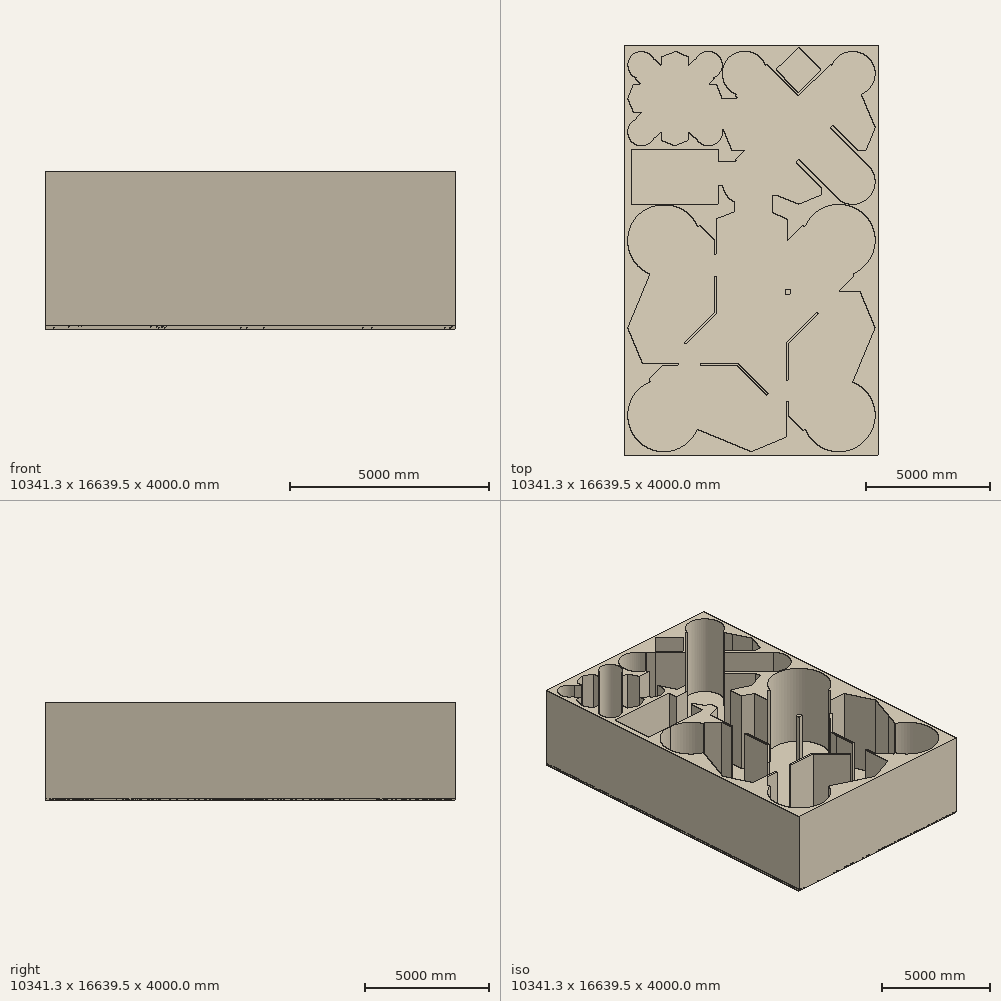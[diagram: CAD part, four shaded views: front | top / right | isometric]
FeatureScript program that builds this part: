
annotation { "Feature Type Name" : "Feature", "Feature Type Description" : "" }
export const myFeature = defineFeature(function(context is Context, id is Id, definition is map)
    precondition{}
    {
        {
            var Q0;
            Q0=qCreatedBy(makeId("Top.planeOp"),FACE);
            var sketch = newSketch(context, id + "F0", { "sketchPlane" : qUnion([Q0])});
            skLineSegment(sketch, "E0", {"start": v(2904.54, 7239.39) * mm, "end": v(3203.1, 7544.71) * mm});
            skLineSegment(sketch, "E1", {"start": v(1018, 2247.97) * mm, "end": v(1926.78, 1871.54) * mm});
            skLineSegment(sketch, "E2", {"start": v(5170.65, 8319.76) * mm, "end": v(-5170.65, 8319.76) * mm});
            skLineSegment(sketch, "E3", {"start": v(-5170.65, 8319.76) * mm, "end": v(-5170.65, -8319.76) * mm});
            skLineSegment(sketch, "E4", {"start": v(-5170.65, -8319.76) * mm, "end": v(5170.65, -8319.76) * mm});
            skLineSegment(sketch, "E5", {"start": v(5170.65, -8319.76) * mm, "end": v(5170.65, 8319.76) * mm});
            skLineSegment(sketch, "E6", {"start": v(-680.22, 1966.34) * mm, "end": v(-680.22, 1871.54) * mm});
            skLineSegment(sketch, "E7", {"start": v(1925.72, 8240.34) * mm, "end": v(2834.63, 7310.89) * mm});
            skLineSegment(sketch, "E8", {"start": v(2834.63, 7310.89) * mm, "end": v(1905.17, 6401.98) * mm});
            skLineSegment(sketch, "E9", {"start": v(1905.17, 6401.98) * mm, "end": v(996.26, 7331.44) * mm});
            skLineSegment(sketch, "E10", {"start": v(996.26, 7331.44) * mm, "end": v(1925.72, 8240.34) * mm});
            skLineSegment(sketch, "E11", {"start": v(4644.22, 4065.52) * mm, "end": v(4321.24, 4065.52) * mm});
            skLineSegment(sketch, "E12", {"start": v(4321.24, 4065.52) * mm, "end": v(4653.11, 4065.52) * mm});
            skLineSegment(sketch, "E13", {"start": v(4653.11, 4065.52) * mm, "end": v(5029.54, 4974.3) * mm});
            skLineSegment(sketch, "E14", {"start": v(5029.54, 4974.3) * mm, "end": v(4644.22, 5883.08) * mm});
            skLineSegment(sketch, "E15", {"start": v(4644.22, 5883.08) * mm, "end": v(4488.3, 6259.5) * mm});
            skLineSegment(sketch, "E16", {"start": v(4488.3, 6259.5) * mm, "end": v(4459.65, 6328.68) * mm});
            skArc(sketch, "E17", {"start": v(4459.65, 6328.68) * mm, "mid": v(4754.48, 7810.89) * mm, "end": v(3272.27, 7516.06) * mm});
            skLineSegment(sketch, "E18", {"start": v(3272.27, 7516.06) * mm, "end": v(3203.1, 7544.71) * mm});
            skLineSegment(sketch, "E19", {"start": v(3203.1, 7544.71) * mm, "end": v(2904.54, 7239.39) * mm});
            skLineSegment(sketch, "E20", {"start": v(2904.54, 7239.39) * mm, "end": v(1903.59, 6260.57) * mm});
            skLineSegment(sketch, "E21", {"start": v(1903.59, 6260.57) * mm, "end": v(924.77, 7261.52) * mm});
            skLineSegment(sketch, "E22", {"start": v(924.77, 7261.52) * mm, "end": v(641.57, 7544.71) * mm});
            skLineSegment(sketch, "E23", {"start": v(641.57, 7544.71) * mm, "end": v(572.4, 7516.06) * mm});
            skArc(sketch, "E24", {"start": v(572.4, 7516.06) * mm, "mid": v(-915.1, 7816.2) * mm, "end": v(-614.98, 6328.68) * mm});
            skLineSegment(sketch, "E25", {"start": v(-614.98, 6328.68) * mm, "end": v(-643.63, 6259.5) * mm});
            skLineSegment(sketch, "E26", {"start": v(-643.63, 6259.5) * mm, "end": v(-543.3, 6159.17) * mm});
            skLineSegment(sketch, "E27", {"start": v(-543.3, 6159.17) * mm, "end": v(-1184.87, 6159.17) * mm});
            skLineSegment(sketch, "E28", {"start": v(-1184.87, 6159.17) * mm, "end": v(-1417.55, 6720.91) * mm});
            skLineSegment(sketch, "E29", {"start": v(-1417.55, 6720.91) * mm, "end": v(-1746.6, 6720.91) * mm});
            skLineSegment(sketch, "E30", {"start": v(-1746.6, 6720.91) * mm, "end": v(-1513.93, 6953.59) * mm});
            skLineSegment(sketch, "E31", {"start": v(-1513.93, 6953.59) * mm, "end": v(-1531.64, 6996.35) * mm});
            skArc(sketch, "E32", {"start": v(-1531.64, 6996.35) * mm, "mid": v(-1349.4, 7912.53) * mm, "end": v(-2265.59, 7730.3) * mm});
            skLineSegment(sketch, "E33", {"start": v(-2265.59, 7730.3) * mm, "end": v(-2308.35, 7748) * mm});
            skLineSegment(sketch, "E34", {"start": v(-2308.35, 7748) * mm, "end": v(-2541.02, 7515.33) * mm});
            skLineSegment(sketch, "E35", {"start": v(-2541.02, 7515.33) * mm, "end": v(-2541.02, 7844.38) * mm});
            skLineSegment(sketch, "E36", {"start": v(-2541.02, 7844.38) * mm, "end": v(-3064.43, 8077.06) * mm});
            skLineSegment(sketch, "E37", {"start": v(-3064.43, 8077.06) * mm, "end": v(-3664.5, 7844.38) * mm});
            skLineSegment(sketch, "E38", {"start": v(-3664.5, 7844.38) * mm, "end": v(-3664.5, 7515.33) * mm});
            skLineSegment(sketch, "E39", {"start": v(-3664.5, 7515.33) * mm, "end": v(-3897.18, 7748) * mm});
            skLineSegment(sketch, "E40", {"start": v(-3897.18, 7748) * mm, "end": v(-3939.94, 7730.3) * mm});
            skArc(sketch, "E41", {"start": v(-3939.94, 7730.3) * mm, "mid": v(-4851.28, 7907.24) * mm, "end": v(-4674.04, 6995.95) * mm});
            skLineSegment(sketch, "E42", {"start": v(-4674.04, 6995.95) * mm, "end": v(-4691.6, 6953.59) * mm});
            skLineSegment(sketch, "E43", {"start": v(-4691.6, 6953.59) * mm, "end": v(-4458.91, 6720.91) * mm});
            skLineSegment(sketch, "E44", {"start": v(-4458.91, 6720.91) * mm, "end": v(-4796.65, 6720.91) * mm});
            skLineSegment(sketch, "E45", {"start": v(-4796.65, 6720.91) * mm, "end": v(-5020.65, 6159.17) * mm});
            skLineSegment(sketch, "E46", {"start": v(-5020.65, 6159.17) * mm, "end": v(-4787.97, 5597.44) * mm});
            skLineSegment(sketch, "E47", {"start": v(-4787.97, 5597.44) * mm, "end": v(-4458.91, 5597.44) * mm});
            skLineSegment(sketch, "E48", {"start": v(-4458.91, 5597.44) * mm, "end": v(-4691.6, 5364.76) * mm});
            skLineSegment(sketch, "E49", {"start": v(-4691.6, 5364.76) * mm, "end": v(-4673.88, 5322) * mm});
            skArc(sketch, "E50", {"start": v(-4673.88, 5322) * mm, "mid": v(-4856.12, 4405.81) * mm, "end": v(-3939.94, 4588.05) * mm});
            skLineSegment(sketch, "E51", {"start": v(-3939.94, 4588.05) * mm, "end": v(-3897.18, 4570.34) * mm});
            skLineSegment(sketch, "E52", {"start": v(-3897.18, 4570.34) * mm, "end": v(-3664.5, 4803.02) * mm});
            skLineSegment(sketch, "E53", {"start": v(-3664.5, 4803.02) * mm, "end": v(-3664.5, 4473.96) * mm});
            skLineSegment(sketch, "E54", {"start": v(-3664.5, 4473.96) * mm, "end": v(-3102.76, 4241.28) * mm});
            skLineSegment(sketch, "E55", {"start": v(-3102.76, 4241.28) * mm, "end": v(-2541.02, 4473.96) * mm});
            skLineSegment(sketch, "E56", {"start": v(-2541.02, 4473.96) * mm, "end": v(-2541.02, 4803.02) * mm});
            skLineSegment(sketch, "E57", {"start": v(-2541.02, 4803.02) * mm, "end": v(-2308.35, 4570.34) * mm});
            skLineSegment(sketch, "E58", {"start": v(-2308.35, 4570.34) * mm, "end": v(-2265.59, 4588.05) * mm});
            skArc(sketch, "E59", {"start": v(-2265.59, 4588.05) * mm, "mid": v(-1544.96, 4276.78) * mm, "end": v(-1184.87, 4974.3) * mm});
            skLineSegment(sketch, "E60", {"start": v(-1184.87, 4974.3) * mm, "end": v(-1175.98, 4974.3) * mm});
            skLineSegment(sketch, "E61", {"start": v(-1175.98, 4974.3) * mm, "end": v(-799.55, 4065.52) * mm});
            skLineSegment(sketch, "E62", {"start": v(-799.55, 4065.52) * mm, "end": v(-267.2, 4065.52) * mm});
            skLineSegment(sketch, "E63", {"start": v(-267.2, 4065.52) * mm, "end": v(-643.63, 3689.1) * mm});
            skLineSegment(sketch, "E64", {"start": v(-643.63, 3689.1) * mm, "end": v(-623.87, 3619.92) * mm});
            skLineSegment(sketch, "E65", {"start": v(-623.87, 3619.92) * mm, "end": v(-1184.87, 3619.92) * mm});
            skLineSegment(sketch, "E66", {"start": v(-1184.87, 3619.92) * mm, "end": v(-1334.87, 3619.92) * mm});
            skLineSegment(sketch, "E67", {"start": v(-1334.87, 3619.92) * mm, "end": v(-1334.87, 4091.28) * mm});
            skLineSegment(sketch, "E68", {"start": v(-1334.87, 4091.28) * mm, "end": v(-4870.65, 4091.28) * mm});
            skLineSegment(sketch, "E69", {"start": v(-4870.65, 4091.28) * mm, "end": v(-4870.65, 1871.54) * mm});
            skLineSegment(sketch, "E70", {"start": v(-4870.65, 1871.54) * mm, "end": v(-1334.87, 1871.54) * mm});
            skLineSegment(sketch, "E71", {"start": v(-1334.87, 1871.54) * mm, "end": v(-1334.87, 2639.74) * mm});
            skLineSegment(sketch, "E72", {"start": v(-1334.87, 2639.74) * mm, "end": v(-1173.94, 2639.74) * mm});
            skArc(sketch, "E73", {"start": v(-1173.94, 2639.74) * mm, "mid": v(-1014.88, 2238.67) * mm, "end": v(-680.22, 1966.34) * mm});
            skLineSegment(sketch, "E74", {"start": v(-680.22, 1966.34) * mm, "end": v(-680.22, 1568.87) * mm});
            skLineSegment(sketch, "E75", {"start": v(-680.22, 1568.87) * mm, "end": v(-1411.63, 1285.27) * mm});
            skLineSegment(sketch, "E76", {"start": v(-1411.63, 1285.27) * mm, "end": v(-1411.63, -165.8) * mm});
            skLineSegment(sketch, "E77", {"start": v(-1411.63, -165.8) * mm, "end": v(-1511.63, -165.8) * mm});
            skLineSegment(sketch, "E78", {"start": v(-1511.63, -165.8) * mm, "end": v(-1511.63, 442.14) * mm});
            skLineSegment(sketch, "E79", {"start": v(-1511.63, 442.14) * mm, "end": v(-2079.62, 1010.13) * mm});
            skLineSegment(sketch, "E80", {"start": v(-2079.62, 1010.13) * mm, "end": v(-2189.27, 964.71) * mm});
            skArc(sketch, "E81", {"start": v(-2189.27, 964.71) * mm, "mid": v(-2692.58, 1598.76) * mm, "end": v(-3464.85, 1841.54) * mm});
            skArc(sketch, "E82", {"start": v(-3464.85, 1841.54) * mm, "mid": v(-4987.75, 718.48) * mm, "end": v(-4113.82, -959.83) * mm});
            skLineSegment(sketch, "E83", {"start": v(-4113.82, -959.83) * mm, "end": v(-4159.24, -1069.49) * mm});
            skLineSegment(sketch, "E84", {"start": v(-4159.24, -1069.49) * mm, "end": v(-4159.24, -1069.49) * mm});
            skLineSegment(sketch, "E85", {"start": v(-4159.24, -1069.49) * mm, "end": v(-4434.25, -1733.43) * mm});
            skLineSegment(sketch, "E86", {"start": v(-4434.25, -1733.43) * mm, "end": v(-5020.65, -3149.11) * mm});
            skLineSegment(sketch, "E87", {"start": v(-5020.65, -3149.11) * mm, "end": v(-4433.78, -4565.94) * mm});
            skLineSegment(sketch, "E88", {"start": v(-4433.78, -4565.94) * mm, "end": v(-2971.24, -4565.94) * mm});
            skLineSegment(sketch, "E89", {"start": v(-2971.24, -4565.94) * mm, "end": v(-2971.24, -4665.94) * mm});
            skLineSegment(sketch, "E90", {"start": v(-2971.24, -4665.94) * mm, "end": v(-3591.24, -4665.94) * mm});
            skLineSegment(sketch, "E91", {"start": v(-3591.24, -4665.94) * mm, "end": v(-4159.24, -5228.73) * mm});
            skLineSegment(sketch, "E92", {"start": v(-4159.24, -5228.73) * mm, "end": v(-4112.88, -5340.67) * mm});
            skArc(sketch, "E93", {"start": v(-4112.88, -5340.67) * mm, "mid": v(-4589.95, -7739.06) * mm, "end": v(-2191.56, -7261.99) * mm});
            skLineSegment(sketch, "E94", {"start": v(-2191.56, -7261.99) * mm, "end": v(-2079.62, -7308.35) * mm});
            skLineSegment(sketch, "E95", {"start": v(-2079.62, -7308.35) * mm, "end": v(-1470.51, -7560.65) * mm});
            skLineSegment(sketch, "E96", {"start": v(-1470.51, -7560.65) * mm, "end": v(0, -8169.76) * mm});
            skLineSegment(sketch, "E97", {"start": v(0, -8169.76) * mm, "end": v(1414.76, -7583.75) * mm});
            skLineSegment(sketch, "E98", {"start": v(1414.76, -7583.75) * mm, "end": v(1414.76, -6110.92) * mm});
            skLineSegment(sketch, "E99", {"start": v(1414.76, -6110.92) * mm, "end": v(1514.76, -6110.92) * mm});
            skLineSegment(sketch, "E100", {"start": v(1514.76, -6110.92) * mm, "end": v(1514.76, -6730.92) * mm});
            skLineSegment(sketch, "E101", {"start": v(1514.76, -6730.92) * mm, "end": v(2079.62, -7308.35) * mm});
            skLineSegment(sketch, "E102", {"start": v(2079.62, -7308.35) * mm, "end": v(2189.28, -7262.93) * mm});
            skArc(sketch, "E103", {"start": v(2189.28, -7262.93) * mm, "mid": v(4591.7, -7740.8) * mm, "end": v(4113.82, -5338.39) * mm});
            skLineSegment(sketch, "E104", {"start": v(4113.82, -5338.39) * mm, "end": v(4159.24, -5228.73) * mm});
            skLineSegment(sketch, "E105", {"start": v(4159.24, -5228.73) * mm, "end": v(4411.54, -4619.62) * mm});
            skLineSegment(sketch, "E106", {"start": v(4411.54, -4619.62) * mm, "end": v(5020.65, -3149.12) * mm});
            skLineSegment(sketch, "E107", {"start": v(5020.65, -3149.12) * mm, "end": v(4411.54, -1678.6) * mm});
            skLineSegment(sketch, "E108", {"start": v(4411.54, -1678.6) * mm, "end": v(3550.14, -1678.6) * mm});
            skLineSegment(sketch, "E109", {"start": v(3550.14, -1678.6) * mm, "end": v(4159.24, -1069.5) * mm});
            skLineSegment(sketch, "E110", {"start": v(4159.24, -1069.5) * mm, "end": v(4113.82, -959.84) * mm});
            skArc(sketch, "E111", {"start": v(4113.82, -959.84) * mm, "mid": v(4591.7, 1442.58) * mm, "end": v(2189.28, 964.71) * mm});
            skLineSegment(sketch, "E112", {"start": v(2189.28, 964.71) * mm, "end": v(2079.62, 1010.13) * mm});
            skLineSegment(sketch, "E113", {"start": v(2079.62, 1010.13) * mm, "end": v(1470.51, 401.03) * mm});
            skLineSegment(sketch, "E114", {"start": v(1470.51, 401.03) * mm, "end": v(1470.51, 1262.43) * mm});
            skLineSegment(sketch, "E115", {"start": v(1470.51, 1262.43) * mm, "end": v(870.54, 1529.15) * mm});
            skLineSegment(sketch, "E116", {"start": v(870.54, 1529.15) * mm, "end": v(870.54, 2239.35) * mm});
            skLineSegment(sketch, "E117", {"start": v(870.54, 2239.35) * mm, "end": v(1009.11, 2247.97) * mm});
            skLineSegment(sketch, "E118", {"start": v(1009.11, 2247.97) * mm, "end": v(1926.78, 1871.54) * mm});
            skLineSegment(sketch, "E119", {"start": v(1926.78, 1871.54) * mm, "end": v(2835.56, 2251.65) * mm});
            skLineSegment(sketch, "E120", {"start": v(2835.56, 2251.65) * mm, "end": v(2826.67, 2568.18) * mm});
            skLineSegment(sketch, "E121", {"start": v(2826.67, 2568.18) * mm, "end": v(1811.82, 3583.03) * mm});
            skLineSegment(sketch, "E122", {"start": v(1811.82, 3583.03) * mm, "end": v(1922.33, 3693.54) * mm});
            skLineSegment(sketch, "E123", {"start": v(1922.33, 3693.54) * mm, "end": v(3525.36, 2081.62) * mm});
            skArc(sketch, "E124", {"start": v(3525.36, 2081.62) * mm, "mid": v(4753.53, 2136.46) * mm, "end": v(4808.38, 3364.63) * mm});
            skLineSegment(sketch, "E125", {"start": v(4808.38, 3364.63) * mm, "end": v(3203.2, 4974.19) * mm});
            skLineSegment(sketch, "E126", {"start": v(3203.2, 4974.19) * mm, "end": v(3309.3, 5080.22) * mm});
            skLineSegment(sketch, "E127", {"start": v(3309.3, 5080.22) * mm, "end": v(4321.24, 4065.52) * mm});
            skLineSegment(sketch, "E128", {"start": v(-2588.42, -3754.54) * mm, "end": v(-2729.84, -3754.54) * mm});
            skLineSegment(sketch, "E129", {"start": v(-2729.84, -3754.54) * mm, "end": v(-2110.7, -3135.4) * mm});
            skLineSegment(sketch, "E130", {"start": v(-2110.7, -3135.4) * mm, "end": v(-1511.62, -2536.32) * mm});
            skLineSegment(sketch, "E131", {"start": v(-1511.62, -2536.32) * mm, "end": v(-1511.62, -1065.8) * mm});
            skLineSegment(sketch, "E132", {"start": v(-1511.62, -1065.8) * mm, "end": v(-1411.62, -1065.8) * mm});
            skLineSegment(sketch, "E133", {"start": v(-1411.62, -1065.8) * mm, "end": v(-1411.62, -2577.74) * mm});
            skLineSegment(sketch, "E134", {"start": v(-1411.62, -2577.74) * mm, "end": v(-2038.33, -3204.44) * mm});
            skLineSegment(sketch, "E135", {"start": v(-2038.33, -3204.44) * mm, "end": v(-2588.42, -3754.54) * mm});
            skLineSegment(sketch, "E136", {"start": v(618.15, -5884.3) * mm, "end": v(-600.22, -4665.94) * mm});
            skLineSegment(sketch, "E137", {"start": v(-600.22, -4665.94) * mm, "end": v(-2071.24, -4665.94) * mm});
            skLineSegment(sketch, "E138", {"start": v(-2071.24, -4665.94) * mm, "end": v(-2071.24, -4565.94) * mm});
            skLineSegment(sketch, "E139", {"start": v(-2071.24, -4565.94) * mm, "end": v(-558.8, -4565.94) * mm});
            skLineSegment(sketch, "E140", {"start": v(-558.8, -4565.94) * mm, "end": v(689.89, -5814.63) * mm});
            skLineSegment(sketch, "E141", {"start": v(689.89, -5814.63) * mm, "end": v(618.15, -5884.3) * mm});
            skLineSegment(sketch, "E142", {"start": v(2662.41, -2500.81) * mm, "end": v(2733.12, -2571.52) * mm});
            skLineSegment(sketch, "E143", {"start": v(2733.12, -2571.52) * mm, "end": v(1514.76, -3789.9) * mm});
            skLineSegment(sketch, "E144", {"start": v(1514.76, -3789.9) * mm, "end": v(1514.76, -5260.47) * mm});
            skLineSegment(sketch, "E145", {"start": v(1514.76, -5260.47) * mm, "end": v(1414.76, -5260.47) * mm});
            skLineSegment(sketch, "E146", {"start": v(1414.76, -5260.47) * mm, "end": v(1414.76, -3748.47) * mm});
            skLineSegment(sketch, "E147", {"start": v(1414.76, -3748.47) * mm, "end": v(2662.41, -2500.81) * mm});
            skLineSegment(sketch, "E148", {"start": v(1380.6, -1574.7) * mm, "end": v(1589.18, -1574.7) * mm});
            skLineSegment(sketch, "E149", {"start": v(1589.18, -1574.7) * mm, "end": v(1589.18, -1774.33) * mm});
            skLineSegment(sketch, "E150", {"start": v(1589.18, -1774.33) * mm, "end": v(1380.6, -1774.33) * mm});
            skLineSegment(sketch, "E151", {"start": v(1380.6, -1774.33) * mm, "end": v(1380.6, -1574.7) * mm});
            skLineSegment(sketch, "E152", {"start": v(-2025.02, -3191.14) * mm, "end": v(-1411.62, -2577.74) * mm});
            skLineSegment(sketch, "E153", {"start": v(-1411.62, -2577.74) * mm, "end": v(-1411.62, -1070.3) * mm});
            skLineSegment(sketch, "E154", {"start": v(-1411.62, -1070.3) * mm, "end": v(-982.34, -1070.3) * mm});
            skLineSegment(sketch, "E155", {"start": v(-982.34, -1070.3) * mm, "end": v(-982.33, -2714.14) * mm});
            skLineSegment(sketch, "E156", {"start": v(-982.33, -2714.14) * mm, "end": v(-1742.18, -3473.98) * mm});
            skLineSegment(sketch, "E157", {"start": v(-1742.18, -3473.98) * mm, "end": v(-2025.02, -3191.14) * mm});
            skLineSegment(sketch, "E158", {"start": v(54.6, -5179.34) * mm, "end": v(340.48, -4893.46) * mm});
            skLineSegment(sketch, "E159", {"start": v(340.48, -4893.46) * mm, "end": v(-387.04, -4165.94) * mm});
            skLineSegment(sketch, "E160", {"start": v(-387.04, -4165.94) * mm, "end": v(-1461.62, -4165.94) * mm});
            skLineSegment(sketch, "E161", {"start": v(-1461.62, -4165.94) * mm, "end": v(-1461.62, -4565.94) * mm});
            skLineSegment(sketch, "E162", {"start": v(-1461.62, -4565.94) * mm, "end": v(-558.8, -4565.94) * mm});
            skLineSegment(sketch, "E163", {"start": v(-558.8, -4565.94) * mm, "end": v(54.6, -5179.34) * mm});
            skLineSegment(sketch, "E164", {"start": v(1408.45, -4623.22) * mm, "end": v(1421.07, -3755.83) * mm});
            skLineSegment(sketch, "E165", {"start": v(1421.07, -3755.83) * mm, "end": v(2528.14, -2635.08) * mm});
            skLineSegment(sketch, "E166", {"start": v(2528.14, -2635.08) * mm, "end": v(2245.16, -2343.74) * mm});
            skLineSegment(sketch, "E167", {"start": v(2245.16, -2343.74) * mm, "end": v(1012.06, -3541.47) * mm});
            skLineSegment(sketch, "E168", {"start": v(1012.06, -3541.47) * mm, "end": v(996.43, -4615.94) * mm});
            skLineSegment(sketch, "E169", {"start": v(996.43, -4615.94) * mm, "end": v(1408.45, -4623.22) * mm});
            skSolve(sketch);
        }
        {
            var Q0;
            Q0=makeQuery(id+"F0.imprint","IMPRINT",FACE,{"disambiguationData":[TD([[makeQuery(id+"F0.imprint","IMPRINT",EDGE,{"derivedFrom":sQuery(id+"F0.wireOp",EDGE,"E2")}),1.0]])]});
            var Q1;
            {var subQ1=sQuery(id+"F0.wireOp",EDGE,"E142");Q1=makeQuery(id+"F0.imprint","IMPRINT",FACE,{"disambiguationData":[TD([[makeQuery(id+"F0.imprint","IMPRINT",EDGE,{"derivedFrom":subQ1}),-1.0]])]});}
            var Q2;
            Q2=makeQuery(id+"F0.imprint","IMPRINT",FACE,{"disambiguationData":[TD([[makeQuery(id+"F0.imprint","IMPRINT",EDGE,{"derivedFrom":sQuery(id+"F0.wireOp",EDGE,"E136")}),-1.0]])]});
            var Q3;
            Q3=makeQuery(id+"F0.imprint","IMPRINT",FACE,{"disambiguationData":[TD([[makeQuery(id+"F0.imprint","IMPRINT",EDGE,{"derivedFrom":sQuery(id+"F0.wireOp",EDGE,"E128")}),-1.0]])]});
            var Q4;
            Q4=makeQuery(id+"F0.imprint","IMPRINT",FACE,{"disambiguationData":[TD([[makeQuery(id+"F0.imprint","IMPRINT",EDGE,{"derivedFrom":sQuery(id+"F0.wireOp",EDGE,"E148")}),-1.0]])]});
            extrude(context, id + "F1", {"entities" : qUnion([Q0, Q1, Q2, Q3, Q4]), "depth" : 4000 * mm, "offsetDistance" : 25 * mm});
        }
        {
            var Q0;
            Q0=makeQuery(id+"F1.opExtrude","SWEPT_FACE",FACE,{"disambiguationData":[OSD([sQuery(id+"F0.wireOp",EDGE,"E5")])]});
            var sketch = newSketch(context, id + "F2", { "sketchPlane" : qUnion([Q0])});
            skLineSegment(sketch, "E170.bottom", {"start": v(-8319.76, 0) * mm, "end": v(8319.76, 0) * mm});
            skLineSegment(sketch, "E170.top", {"start": v(-8319.76, 100) * mm, "end": v(8319.76, 100) * mm});
            skLineSegment(sketch, "E170.left", {"start": v(-8319.76, 0) * mm, "end": v(-8319.76, 100) * mm});
            skLineSegment(sketch, "E170.right", {"start": v(8319.76, 0) * mm, "end": v(8319.76, 100) * mm});
            skSolve(sketch);
        }
        {
            var Q0;
            Q0 = qSketchRegion(id + "F2", true);
            var Q1;
            Q1=makeQuery(id+"F1.opExtrude","SWEPT_FACE",FACE,{"disambiguationData":[OSD([sQuery(id+"F0.wireOp",EDGE,"E3")])]});
            extrude(context, id + "F3", {"entities" : qUnion([Q0]), "endBound" : BoundingType.UP_TO_SURFACE, "oppositeDirection" : true, "depth" : 12400 * mm, "endBoundEntityFace" : qUnion([Q1]), "offsetDistance" : 25 * mm});
        }
    });
